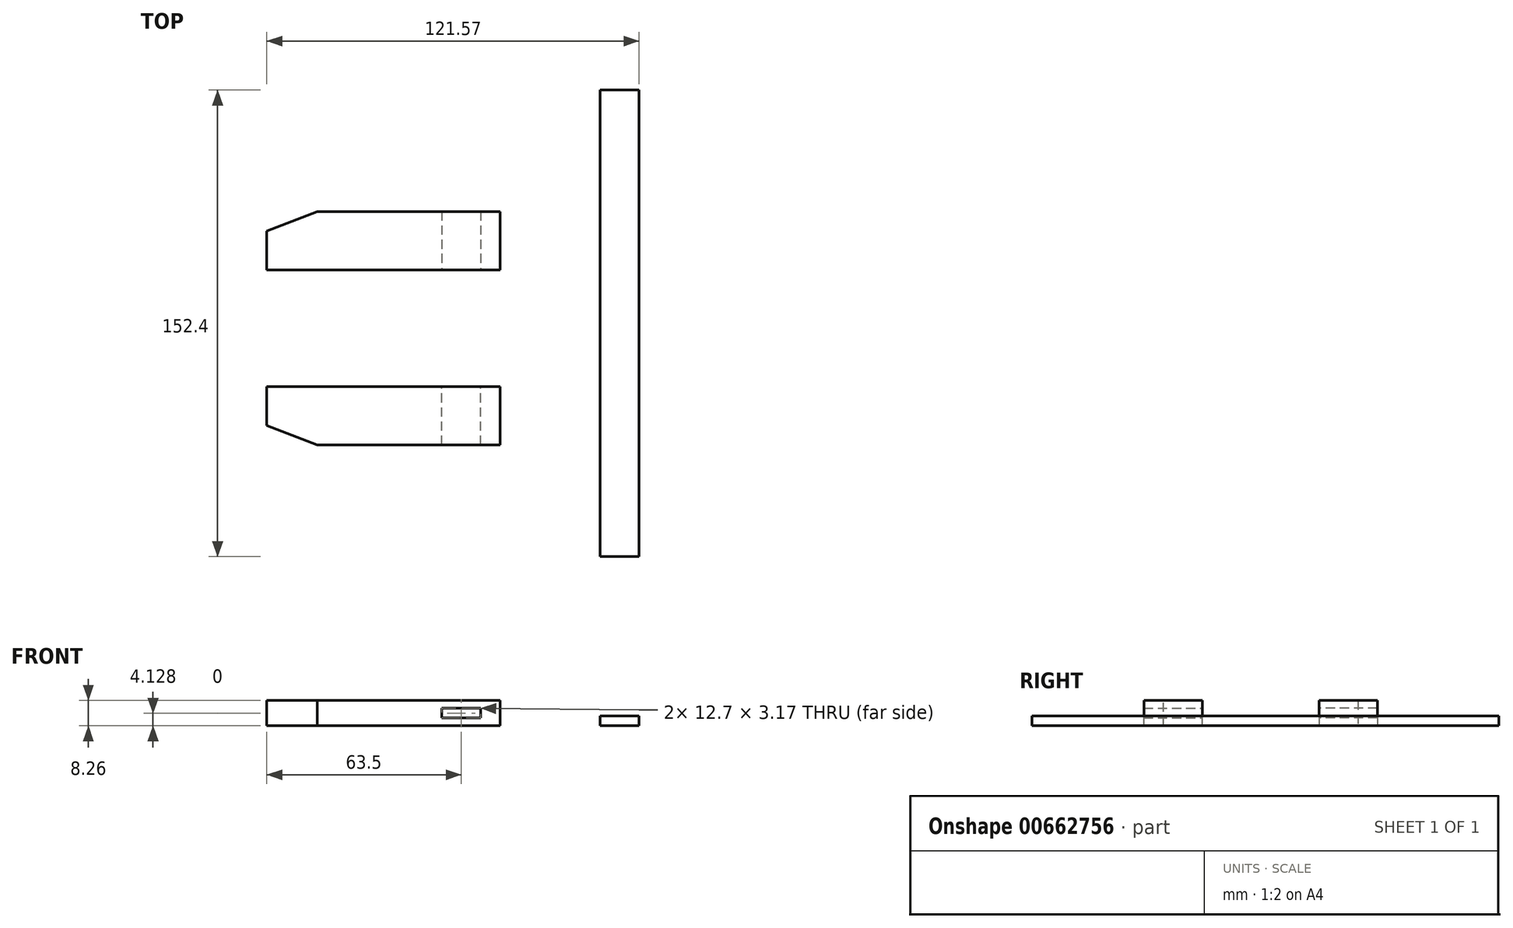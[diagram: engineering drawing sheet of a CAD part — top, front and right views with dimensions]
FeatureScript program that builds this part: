
annotation { "Feature Type Name" : "Feature", "Feature Type Description" : "" }
export const myFeature = defineFeature(function(context is Context, id is Id, definition is map)
    precondition{}
    {
        {
            var Q0;
            Q0=qCreatedBy(makeId("Top.planeOp"),FACE);
            var sketch = newSketch(context, id + "F0", { "sketchPlane" : qUnion([Q0])});
            skLineSegment(sketch, "E0.bottom", {"start": v(40.19, 97.46) * mm, "end": v(52.89, 97.46) * mm});
            skLineSegment(sketch, "E0.top", {"start": v(40.19, -54.94) * mm, "end": v(52.89, -54.94) * mm});
            skLineSegment(sketch, "E0.left", {"start": v(40.19, 97.46) * mm, "end": v(40.19, -54.94) * mm});
            skLineSegment(sketch, "E0.right", {"start": v(52.89, 97.46) * mm, "end": v(52.89, -54.94) * mm});
            skSolve(sketch);
        }
        {
            var Q0;
            Q0 = qSketchRegion(id + "F0", true);
            extrude(context, id + "F1", {"entities" : qUnion([Q0]), "depth" : 3.17 * mm, "offsetDistance" : 25.4 * mm});
        }
        {
            var Q0;
            Q0=qCreatedBy(makeId("Top.planeOp"),FACE);
            var sketch = newSketch(context, id + "F2", { "sketchPlane" : qUnion([Q0])});
            skLineSegment(sketch, "E1.bottom", {"start": v(-68.68, 38.74) * mm, "end": v(7.52, 38.74) * mm});
            skLineSegment(sketch, "E1.top", {"start": v(-52.17, 57.79) * mm, "end": v(7.52, 57.79) * mm});
            skLineSegment(sketch, "E1.left", {"start": v(-68.68, 38.74) * mm, "end": v(-68.68, 51.44) * mm});
            skLineSegment(sketch, "E1.right", {"start": v(7.52, 38.74) * mm, "end": v(7.52, 57.79) * mm});
            skLineSegment(sketch, "E2", {"start": v(-68.68, 51.44) * mm, "end": v(-52.17, 57.79) * mm});
            skPoint(sketch, "E3.bottom.end.orphan", {"position": v(-52.17, 51.44) * mm});
            skPoint(sketch, "E4.orphan", {"position": v(-68.68, 57.79) * mm});
            skSolve(sketch);
        }
        {
            var Q0;
            Q0 = qSketchRegion(id + "F2", true);
            extrude(context, id + "F3", {"entities" : qUnion([Q0]), "depth" : 8.25 * mm, "offsetDistance" : 25.4 * mm});
        }
        {
            var Q0;
            Q0=makeQuery(id+"F3.opExtrude","SWEPT_FACE",FACE,{"disambiguationData":[OSD([sQuery(id+"F2.wireOp",EDGE,"E1.bottom")])]});
            var sketch = newSketch(context, id + "F4", { "sketchPlane" : qUnion([Q0])});
            skLineSegment(sketch, "E5.bottom", {"start": v(-11.53, 5.72) * mm, "end": v(1.17, 5.72) * mm});
            skLineSegment(sketch, "E5.top", {"start": v(-11.53, 2.54) * mm, "end": v(1.17, 2.54) * mm});
            skLineSegment(sketch, "E5.left", {"start": v(-11.53, 5.72) * mm, "end": v(-11.53, 2.54) * mm});
            skLineSegment(sketch, "E5.right", {"start": v(1.17, 5.72) * mm, "end": v(1.17, 2.54) * mm});
            skSolve(sketch);
        }
        {
            var Q0;
            Q0 = qSketchRegion(id + "F4", true);
            extrude(context, id + "F5", {"entities" : qUnion([Q0]), "operationType" : NewBodyOperationType.REMOVE, "oppositeDirection" : true, "depth" : 25.4 * mm, "offsetDistance" : 25.4 * mm});
        }
        {
            var Q0;
            Q0=makeQuery(id+"F3.opExtrude","SWEPT_BODY",BODY,{"disambiguationData":[OSD([sQuery(id+"F2.wireOp",EDGE,"E1.bottom"),sQuery(id+"F2.wireOp",EDGE,"E1.top"),sQuery(id+"F2.wireOp",EDGE,"E1.left"),sQuery(id+"F2.wireOp",EDGE,"E1.right"),sQuery(id+"F2.wireOp",EDGE,"E2")])]});
            transform(context, id + "F6", {"entities" : qUnion([Q0]), "transformType" : TransformType.COPY});
        }
        {
            var Q0;
            Q0=makeQuery(id+"F6.opPattern","COPY",BODY,{"derivedFrom":makeQuery(id+"F3.opExtrude","SWEPT_BODY",BODY,{"disambiguationData":[OSD([sQuery(id+"F2.wireOp",EDGE,"E1.bottom"),sQuery(id+"F2.wireOp",EDGE,"E1.top"),sQuery(id+"F2.wireOp",EDGE,"E1.left"),sQuery(id+"F2.wireOp",EDGE,"E1.right"),sQuery(id+"F2.wireOp",EDGE,"E2")])]}),"instanceName":"1"});
            transform(context, id + "F7", {"entities" : qUnion([Q0]), "transformType" : TransformType.TRANSLATION_3D, "dx" : 0 * mm, "dy" : -76.2 * mm, "dz" : 0 * mm, "makeCopy" : false});
        }
        {
            var Q0;
            Q0=makeQuery(id+"F6.opPattern","COPY",BODY,{"derivedFrom":makeQuery(id+"F3.opExtrude","SWEPT_BODY",BODY,{"disambiguationData":[OSD([sQuery(id+"F2.wireOp",EDGE,"E1.bottom"),sQuery(id+"F2.wireOp",EDGE,"E1.top"),sQuery(id+"F2.wireOp",EDGE,"E1.left"),sQuery(id+"F2.wireOp",EDGE,"E1.right"),sQuery(id+"F2.wireOp",EDGE,"E2")])]}),"instanceName":"1"});
            var Q1;
            Q1=makeQuery(id+"F6.opPattern","COPY",EDGE,{"derivedFrom":makeQuery(id+"F3.opExtrude","CAP_EDGE",EDGE,{"disambiguationData":[OSD([sQuery(id+"F2.wireOp",EDGE,"E1.top")])],"isStart":false}),"instanceName":"1"});
            transform(context, id + "F8", {"entities" : qUnion([Q0]), "transformType" : TransformType.ROTATION, "transformAxis" : qUnion([Q1]), "angle" : 180 * degree, "makeCopy" : false});
        }
        {
            var Q0;
            Q0=makeQuery(id+"F6.opPattern","COPY",BODY,{"derivedFrom":makeQuery(id+"F3.opExtrude","SWEPT_BODY",BODY,{"disambiguationData":[OSD([sQuery(id+"F2.wireOp",EDGE,"E1.bottom"),sQuery(id+"F2.wireOp",EDGE,"E1.top"),sQuery(id+"F2.wireOp",EDGE,"E1.left"),sQuery(id+"F2.wireOp",EDGE,"E1.right"),sQuery(id+"F2.wireOp",EDGE,"E2")])]}),"instanceName":"1"});
            transform(context, id + "F9", {"entities" : qUnion([Q0]), "transformType" : TransformType.TRANSLATION_3D, "dx" : 0 * mm, "dy" : 0 * mm, "dz" : -8.25 * mm, "makeCopy" : false});
        }
    });
